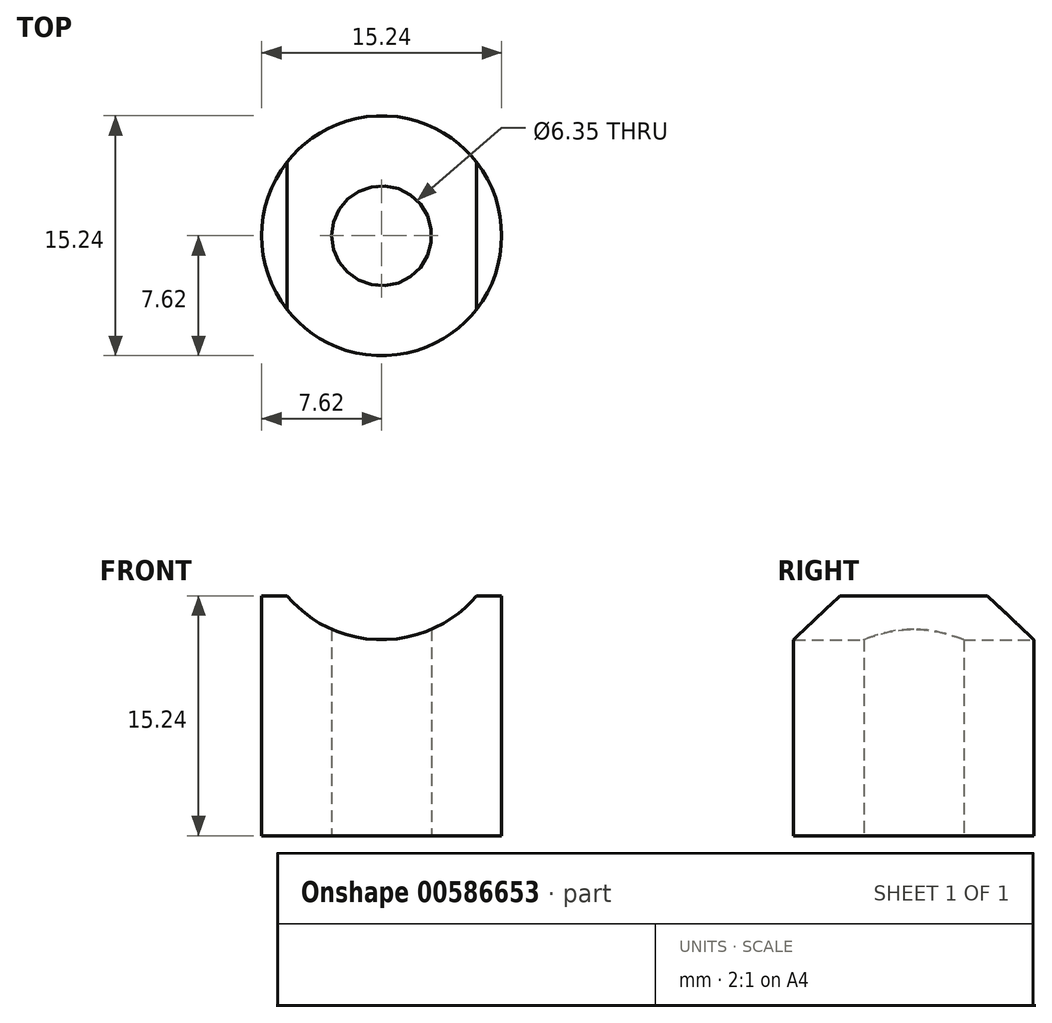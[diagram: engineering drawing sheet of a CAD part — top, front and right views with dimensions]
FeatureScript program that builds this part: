
annotation { "Feature Type Name" : "Feature", "Feature Type Description" : "" }
export const myFeature = defineFeature(function(context is Context, id is Id, definition is map)
    precondition{}
    {
        {
            var Q0;
            Q0=qCreatedBy(makeId("Top.planeOp"),FACE);
            var sketch = newSketch(context, id + "F0", { "sketchPlane" : qUnion([Q0])});
            skCircle(sketch, "E0", {"center": v(0, 0) * mm, "radius": 7.62 * mm});
            skCircle(sketch, "E1", {"center": v(0, 0) * mm, "radius": 3.18 * mm});
            skSolve(sketch);
        }
        {
            var Q0;
            Q0=makeQuery(id+"F0.imprint","IMPRINT",FACE,{"disambiguationData":[TD([[makeQuery(id+"F0.imprint","IMPRINT",EDGE,{"derivedFrom":sQuery(id+"F0.wireOp",EDGE,"E0")}),1.0]])]});
            extrude(context, id + "F1", {"entities" : qUnion([Q0]), "depth" : 15.24 * mm, "offsetDistance" : 25.4 * mm});
        }
        {
            var Q0;
            Q0=qCreatedBy(makeId("Front.planeOp"),FACE);
            var sketch = newSketch(context, id + "F2", { "sketchPlane" : qUnion([Q0])});
            skCircle(sketch, "E2", {"center": v(0, 20.32) * mm, "radius": 7.87 * mm});
            skSolve(sketch);
        }
        {
            var Q0;
            Q0 = qSketchRegion(id + "F2", true);
            extrude(context, id + "F3", {"entities" : qUnion([Q0]), "operationType" : NewBodyOperationType.REMOVE, "endBound" : BoundingType.SYMMETRIC, "depth" : 25.4 * mm, "offsetDistance" : 25.4 * mm});
        }
    });
